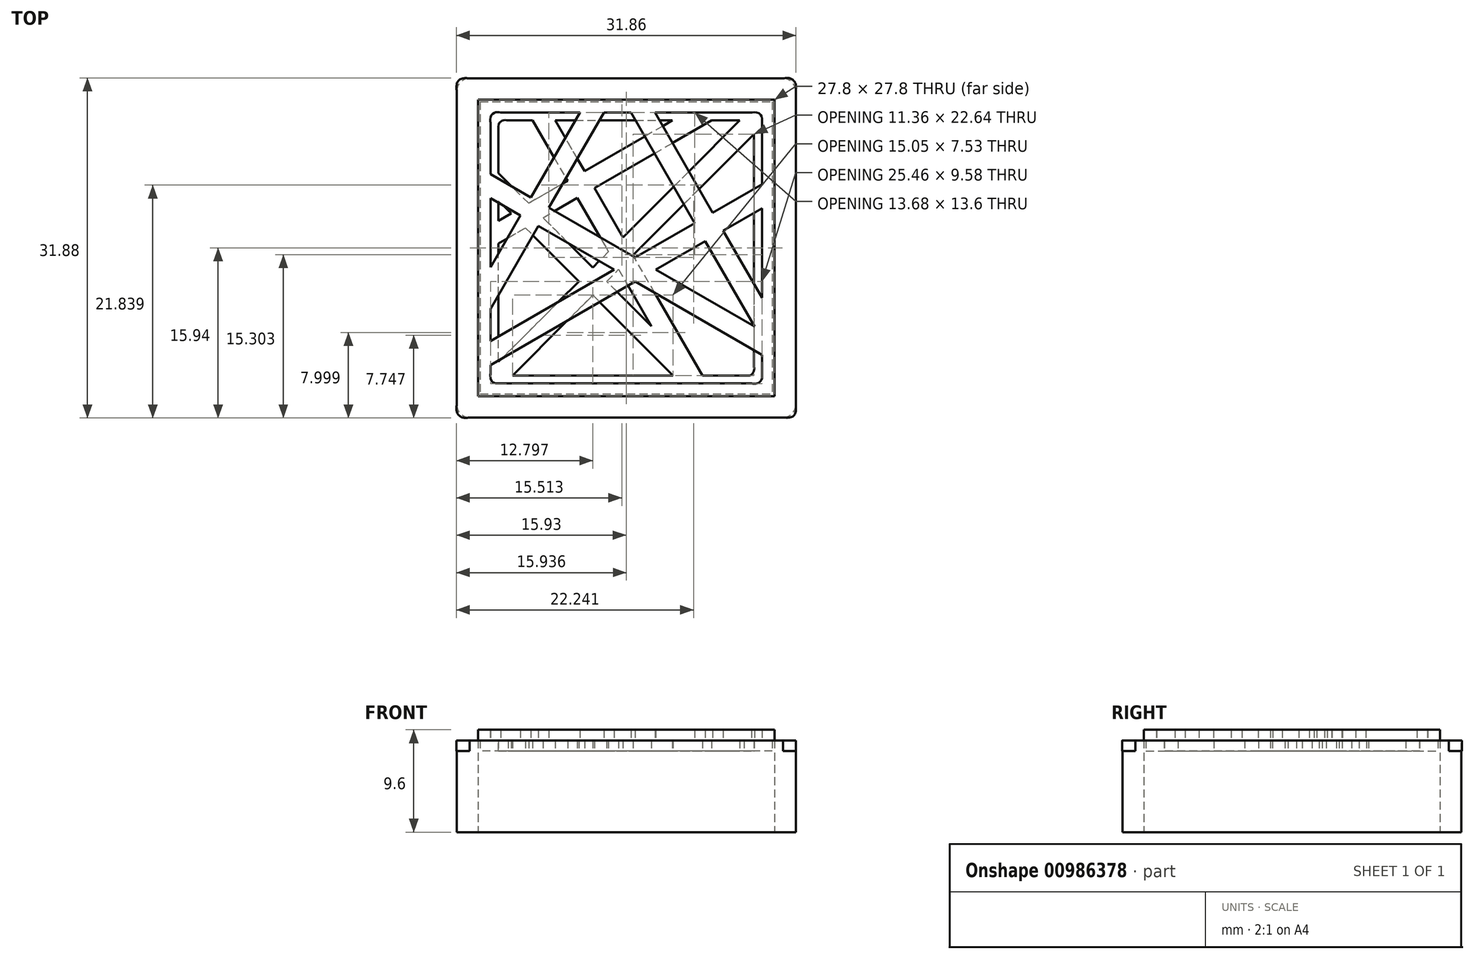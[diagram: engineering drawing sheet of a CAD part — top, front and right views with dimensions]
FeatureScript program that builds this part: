
annotation { "Feature Type Name" : "Feature", "Feature Type Description" : "" }
export const myFeature = defineFeature(function(context is Context, id is Id, definition is map)
    precondition{}
    {
        {
            var Q0;
            Q0=qCreatedBy(makeId("Top.planeOp"),FACE);
            var sketch = newSketch(context, id + "F0", { "sketchPlane" : qUnion([Q0])});
            skLineSegment(sketch, "E0", {"start": v(-12.72, 4.67) * mm, "end": v(-9.92, 3.05) * mm});
            skLineSegment(sketch, "E1", {"start": v(-9.92, 3.05) * mm, "end": v(-12.72, -1.8) * mm});
            skLineSegment(sketch, "E2", {"start": v(-12.72, -1.8) * mm, "end": v(-12.72, 4.67) * mm});
            skLineSegment(sketch, "E3", {"start": v(-12.72, -5.7) * mm, "end": v(-8.23, 2.08) * mm});
            skLineSegment(sketch, "E4", {"start": v(-8.23, 2.08) * mm, "end": v(-1.12, -2.03) * mm});
            skLineSegment(sketch, "E5", {"start": v(-1.12, -2.03) * mm, "end": v(-12.72, -8.72) * mm});
            skLineSegment(sketch, "E6", {"start": v(-12.72, -8.72) * mm, "end": v(-12.72, -5.7) * mm});
            skLineSegment(sketch, "E7", {"start": v(-7.26, 3.76) * mm, "end": v(-2.1, 12.7) * mm});
            skLineSegment(sketch, "E8", {"start": v(-2.1, 12.7) * mm, "end": v(0.44, 12.7) * mm});
            skLineSegment(sketch, "E9", {"start": v(0.44, 12.7) * mm, "end": v(6.43, 2.33) * mm});
            skLineSegment(sketch, "E10", {"start": v(6.43, 2.33) * mm, "end": v(0.82, -0.9) * mm});
            skLineSegment(sketch, "E11", {"start": v(0.82, -0.9) * mm, "end": v(-7.26, 3.76) * mm});
            skLineSegment(sketch, "E12", {"start": v(7.4, 0.64) * mm, "end": v(12.03, -7.37) * mm});
            skLineSegment(sketch, "E13", {"start": v(12.03, -7.37) * mm, "end": v(2.77, -2.03) * mm});
            skLineSegment(sketch, "E14", {"start": v(2.77, -2.03) * mm, "end": v(7.4, 0.64) * mm});
            skLineSegment(sketch, "E15", {"start": v(9.09, 1.62) * mm, "end": v(12.72, 3.72) * mm});
            skLineSegment(sketch, "E16", {"start": v(12.72, 3.72) * mm, "end": v(12.72, -4.68) * mm});
            skLineSegment(sketch, "E17", {"start": v(12.72, -4.68) * mm, "end": v(9.09, 1.62) * mm});
            skFitSpline(sketch, "E18", {"points": [v(12.72, 11.74) * mm, v(12.72, 11.74) * mm, v(12.72, 11.74) * mm, v(12.72, 11.6) * mm, v(12.72, 6.12) * mm, v(12.72, 5.97) * mm, v(12.72, 5.97) * mm, v(12.72, 5.97) * mm]});
            skFitSpline(sketch, "E19", {"points": [v(12.72, 5.97) * mm, v(12.72, 5.97) * mm, v(12.72, 5.97) * mm, v(12.6, 5.9) * mm, v(8.23, 3.37) * mm, v(8.11, 3.3) * mm, v(8.11, 3.3) * mm, v(8.11, 3.3) * mm]});
            skFitSpline(sketch, "E20", {"points": [v(8.11, 3.3) * mm, v(8.11, 3.3) * mm, v(8.11, 3.3) * mm, v(8.04, 3.43) * mm, v(6.72, 5.73) * mm, v(5.4, 8) * mm]});
            skFitSpline(sketch, "E21", {"points": [v(5.4, 8) * mm, v(4.09, 10.28) * mm, v(2.76, 12.58) * mm, v(2.7, 12.7) * mm, v(2.7, 12.7) * mm, v(2.7, 12.7) * mm]});
            skFitSpline(sketch, "E22", {"points": [v(2.7, 12.7) * mm, v(2.7, 12.7) * mm, v(2.7, 12.7) * mm, v(2.93, 12.7) * mm, v(11.72, 12.7) * mm, v(11.76, 12.7) * mm, v(11.77, 12.7) * mm, v(12.3, 12.7) * mm, v(12.72, 12.27) * mm, v(12.72, 11.74) * mm]});
            skFitSpline(sketch, "E23", {"points": [v(-11.76, 12.7) * mm, v(-11.76, 12.7) * mm, v(-11.76, 12.7) * mm, v(-11.57, 12.7) * mm, v(-4.54, 12.7) * mm, v(-4.35, 12.7) * mm, v(-4.35, 12.7) * mm, v(-4.35, 12.7) * mm]});
            skFitSpline(sketch, "E24", {"points": [v(-4.35, 12.7) * mm, v(-4.35, 12.7) * mm, v(-4.35, 12.7) * mm, v(-4.47, 12.5) * mm, v(-8.83, 4.94) * mm, v(-8.95, 4.74) * mm, v(-8.95, 4.74) * mm, v(-8.95, 4.74) * mm]});
            skFitSpline(sketch, "E25", {"points": [v(-8.95, 4.74) * mm, v(-8.95, 4.74) * mm, v(-8.95, 4.74) * mm, v(-9, 4.77) * mm, v(-9.92, 5.3) * mm, v(-10.84, 5.83) * mm]});
            skFitSpline(sketch, "E26", {"points": [v(-10.84, 5.83) * mm, v(-11.75, 6.36) * mm, v(-12.68, 6.9) * mm, v(-12.72, 6.92) * mm, v(-12.72, 6.92) * mm, v(-12.72, 6.92) * mm]});
            skFitSpline(sketch, "E27", {"points": [v(-12.72, 6.92) * mm, v(-12.72, 6.92) * mm, v(-12.72, 6.92) * mm, v(-12.72, 7.04) * mm, v(-12.72, 11.72) * mm, v(-12.72, 11.74) * mm, v(-12.72, 11.74) * mm, v(-12.72, 12.27) * mm, v(-12.29, 12.7) * mm, v(-11.76, 12.7) * mm]});
            skFitSpline(sketch, "E28", {"points": [v(11.76, -12.7) * mm, v(11.76, -12.7) * mm, v(11.76, -12.7) * mm, v(11.45, -12.7) * mm, v(-11.64, -12.7) * mm, v(-11.76, -12.7) * mm, v(-11.76, -12.7) * mm, v(-12.3, -12.7) * mm, v(-12.72, -12.27) * mm, v(-12.72, -11.74) * mm, v(-12.72, -11.74) * mm, v(-12.72, -11.73) * mm, v(-12.72, -11.05) * mm, v(-12.72, -10.98) * mm, v(-12.72, -10.98) * mm, v(-12.72, -10.97) * mm]});
            skFitSpline(sketch, "E29", {"points": [v(-12.72, -10.97) * mm, v(-12.72, -10.97) * mm, v(-12.72, -10.97) * mm, v(-12.64, -10.92) * mm, v(-9.28, -8.99) * mm, v(-5.95, -7.06) * mm]});
            skFitSpline(sketch, "E30", {"points": [v(-5.95, -7.06) * mm, v(-2.62, -5.14) * mm, v(0.74, -3.2) * mm, v(0.82, -3.15) * mm, v(0.82, -3.15) * mm, v(0.82, -3.15) * mm]});
            skFitSpline(sketch, "E31", {"points": [v(0.82, -3.15) * mm, v(0.82, -3.15) * mm, v(0.82, -3.15) * mm, v(0.98, -3.24) * mm, v(12.57, -9.93) * mm, v(12.72, -10.02) * mm, v(12.72, -10.02) * mm, v(12.72, -10.02) * mm]});
            skFitSpline(sketch, "E32", {"points": [v(12.72, -10.02) * mm, v(12.72, -10.02) * mm, v(12.72, -10.02) * mm, v(12.72, -10.11) * mm, v(12.72, -11.73) * mm, v(12.72, -11.74) * mm, v(12.72, -11.74) * mm, v(12.72, -12.27) * mm, v(12.29, -12.7) * mm, v(11.76, -12.7) * mm]});
            skLineSegment(sketch, "E33.bottom", {"start": v(-13.9, 15.9) * mm, "end": v(13.9, 15.9) * mm});
            skLineSegment(sketch, "E33.top", {"start": v(-13.9, -15.9) * mm, "end": v(13.9, -15.9) * mm});
            skLineSegment(sketch, "E33.left", {"start": v(-15.9, 13.9) * mm, "end": v(-15.9, -13.9) * mm});
            skLineSegment(sketch, "E33.right", {"start": v(15.9, 13.9) * mm, "end": v(15.9, -13.9) * mm});
            skPoint(sketch, "E33.middle", {"position": v(0, 0) * mm});
            skPoint(sketch, "E34.visualSharp", {"position": v(-15.9, 15.9) * mm});
            skArc(sketch, "E34.filletArc", {"start": v(-13.9, 15.9) * mm, "mid": v(-15.31, 15.31) * mm, "end": v(-15.9, 13.9) * mm});
            skPoint(sketch, "E35.visualSharp", {"position": v(15.9, 15.9) * mm});
            skArc(sketch, "E35.filletArc", {"start": v(15.9, 13.9) * mm, "mid": v(15.31, 15.31) * mm, "end": v(13.9, 15.9) * mm});
            skPoint(sketch, "E36.visualSharp", {"position": v(15.9, -15.9) * mm});
            skArc(sketch, "E36.filletArc", {"start": v(13.9, -15.9) * mm, "mid": v(15.31, -15.31) * mm, "end": v(15.9, -13.9) * mm});
            skPoint(sketch, "E37.visualSharp", {"position": v(-15.9, -15.9) * mm});
            skArc(sketch, "E37.filletArc", {"start": v(-15.9, -13.9) * mm, "mid": v(-15.31, -15.31) * mm, "end": v(-13.9, -15.9) * mm});
            skSolve(sketch);
        }
        {
            var Q0;
            Q0=makeQuery(id+"F0.imprint","IMPRINT",FACE,{"disambiguationData":[TD([[makeQuery(id+"F0.imprint","IMPRINT",EDGE,{"derivedFrom":sQuery(id+"F0.wireOp",EDGE,"E0")}),1.0]])]});
            extrude(context, id + "F1", {"entities" : qUnion([Q0]), "depth" : 9.6 * mm, "offsetDistance" : 25 * mm, "hasSecondDirection" : true, "secondDirectionOppositeDirection" : false, "secondDirectionDepth" : 8.6 * mm});
        }
        {
            var Q0;
            Q0=qCreatedBy(makeId("Top.planeOp"),FACE);
            var sketch = newSketch(context, id + "F2", { "sketchPlane" : qUnion([Q0])});
            skLineSegment(sketch, "E38", {"start": v(-11.98, 4.42) * mm, "end": v(-10.79, 3.23) * mm});
            skLineSegment(sketch, "E39", {"start": v(-10.79, 3.23) * mm, "end": v(-11.98, 2.54) * mm});
            skLineSegment(sketch, "E40", {"start": v(-11.98, 2.54) * mm, "end": v(-11.98, 4.42) * mm});
            skLineSegment(sketch, "E41", {"start": v(-11.98, 0.42) * mm, "end": v(-9.45, 1.88) * mm});
            skLineSegment(sketch, "E42", {"start": v(-9.45, 1.88) * mm, "end": v(-4.43, -3.13) * mm});
            skLineSegment(sketch, "E43", {"start": v(-4.43, -3.13) * mm, "end": v(-11.98, -10.68) * mm});
            skLineSegment(sketch, "E44", {"start": v(-11.98, -10.68) * mm, "end": v(-11.98, 0.42) * mm});
            skLineSegment(sketch, "E45", {"start": v(-3.13, -4.43) * mm, "end": v(4.4, -11.96) * mm});
            skLineSegment(sketch, "E46", {"start": v(4.4, -11.96) * mm, "end": v(-10.66, -11.96) * mm});
            skLineSegment(sketch, "E47", {"start": v(-10.66, -11.96) * mm, "end": v(-3.13, -4.43) * mm});
            skLineSegment(sketch, "E48", {"start": v(-1.84, -3.13) * mm, "end": v(-0.71, -2) * mm});
            skLineSegment(sketch, "E49", {"start": v(-0.71, -2) * mm, "end": v(2.36, -7.33) * mm});
            skLineSegment(sketch, "E50", {"start": v(2.36, -7.33) * mm, "end": v(-1.84, -3.13) * mm});
            skLineSegment(sketch, "E51", {"start": v(-3.13, -1.84) * mm, "end": v(-7.8, 2.83) * mm});
            skLineSegment(sketch, "E52", {"start": v(-7.8, 2.83) * mm, "end": v(-4.58, 4.7) * mm});
            skLineSegment(sketch, "E53", {"start": v(-4.58, 4.7) * mm, "end": v(-1.66, -0.36) * mm});
            skLineSegment(sketch, "E54", {"start": v(-1.66, -0.36) * mm, "end": v(-3.13, -1.84) * mm});
            skLineSegment(sketch, "E55", {"start": v(-3, 5.61) * mm, "end": v(8, 11.96) * mm});
            skLineSegment(sketch, "E56", {"start": v(8, 11.96) * mm, "end": v(10.66, 11.96) * mm});
            skLineSegment(sketch, "E57", {"start": v(10.66, 11.96) * mm, "end": v(-0.32, 0.98) * mm});
            skLineSegment(sketch, "E58", {"start": v(-0.32, 0.98) * mm, "end": v(-3, 5.61) * mm});
            skLineSegment(sketch, "E59", {"start": v(-3.9, 7.2) * mm, "end": v(-6.66, 11.96) * mm});
            skLineSegment(sketch, "E60", {"start": v(-6.66, 11.96) * mm, "end": v(4.33, 11.96) * mm});
            skLineSegment(sketch, "E61", {"start": v(4.33, 11.96) * mm, "end": v(-3.9, 7.2) * mm});
            skFitSpline(sketch, "E62", {"points": [v(14.7, 15.9) * mm, v(14.7, 15.9) * mm, v(14.7, 15.9) * mm, v(14.31, 15.9) * mm, v(-14.62, 15.9) * mm, v(-14.7, 15.9) * mm, v(-14.7, 15.9) * mm, v(-15.36, 15.9) * mm, v(-15.9, 15.36) * mm, v(-15.9, 14.7) * mm, v(-15.9, 14.7) * mm, v(-15.9, 14.62) * mm, v(-15.9, -14.64) * mm, v(-15.9, -14.7) * mm, v(-15.9, -14.7) * mm, v(-15.9, -15.36) * mm, v(-15.36, -15.9) * mm, v(-14.7, -15.9) * mm]});
            skFitSpline(sketch, "E63", {"points": [v(-14.7, -15.9) * mm, v(-14.7, -15.9) * mm, v(-14.7, -15.9) * mm, v(-14.31, -15.9) * mm, v(14.62, -15.9) * mm, v(14.7, -15.9) * mm, v(14.7, -15.9) * mm, v(15.36, -15.9) * mm, v(15.9, -15.36) * mm, v(15.9, -14.7) * mm, v(15.9, -14.7) * mm, v(15.9, -14.62) * mm, v(15.9, 14.64) * mm, v(15.9, 14.7) * mm, v(15.9, 14.7) * mm, v(15.9, 15.36) * mm, v(15.36, 15.9) * mm, v(14.7, 15.9) * mm]});
            skFitSpline(sketch, "E64", {"points": [v(-11.07, 11.96) * mm, v(-11.07, 11.96) * mm, v(-11.07, 11.96) * mm, v(-10.95, 11.96) * mm, v(-8.89, 11.96) * mm, v(-8.78, 11.96) * mm, v(-8.78, 11.96) * mm, v(-8.77, 11.96) * mm]});
            skFitSpline(sketch, "E65", {"points": [v(-8.77, 11.96) * mm, v(-8.77, 11.96) * mm, v(-8.77, 11.96) * mm, v(-8.7, 11.81) * mm, v(-5.58, 6.43) * mm, v(-5.5, 6.28) * mm, v(-5.5, 6.28) * mm, v(-5.5, 6.28) * mm]});
            skFitSpline(sketch, "E66", {"points": [v(-5.5, 6.28) * mm, v(-5.5, 6.28) * mm, v(-5.5, 6.28) * mm, v(-5.6, 6.23) * mm, v(-9.05, 4.23) * mm, v(-9.14, 4.18) * mm, v(-9.14, 4.18) * mm, v(-9.15, 4.18) * mm]});
            skFitSpline(sketch, "E67", {"points": [v(-9.15, 4.18) * mm, v(-9.15, 4.18) * mm, v(-9.15, 4.18) * mm, v(-9.22, 4.25) * mm, v(-11.9, 6.94) * mm, v(-11.98, 7) * mm, v(-11.98, 7) * mm, v(-11.98, 7) * mm]});
            skFitSpline(sketch, "E68", {"points": [v(-11.98, 7) * mm, v(-11.98, 7.01) * mm, v(-11.98, 7.01) * mm, v(-11.98, 7.11) * mm, v(-11.98, 11.03) * mm, v(-11.98, 11.05) * mm, v(-11.98, 11.05) * mm, v(-11.97, 11.55) * mm, v(-11.57, 11.96) * mm, v(-11.07, 11.96) * mm]});
            skFitSpline(sketch, "E69", {"points": [v(11.07, -11.96) * mm, v(11.07, -11.96) * mm, v(11.07, -11.96) * mm, v(10.97, -11.96) * mm, v(7.25, -11.96) * mm, v(7.15, -11.96) * mm, v(7.15, -11.96) * mm, v(7.15, -11.96) * mm]});
            skFitSpline(sketch, "E70", {"points": [v(7.15, -11.96) * mm, v(7.15, -11.96) * mm, v(7.15, -11.96) * mm, v(7.07, -11.81) * mm, v(0.72, -0.81) * mm, v(0.63, -0.67) * mm, v(0.63, -0.67) * mm, v(0.63, -0.67) * mm]});
            skFitSpline(sketch, "E71", {"points": [v(0.63, -0.67) * mm, v(0.63, -0.67) * mm, v(0.63, -0.67) * mm, v(0.7, -0.6) * mm, v(3.51, 2.22) * mm, v(6.3, 5) * mm]});
            skFitSpline(sketch, "E72", {"points": [v(6.3, 5) * mm, v(9.1, 7.8) * mm, v(11.9, 10.6) * mm, v(11.98, 10.68) * mm, v(11.98, 10.68) * mm, v(11.98, 10.68) * mm]});
            skFitSpline(sketch, "E73", {"points": [v(11.98, 10.68) * mm, v(11.98, 10.68) * mm, v(11.98, 10.68) * mm, v(11.98, 10.4) * mm, v(11.98, -10.96) * mm, v(11.98, -11.05) * mm, v(11.98, -11.05) * mm, v(11.97, -11.55) * mm, v(11.57, -11.96) * mm, v(11.07, -11.96) * mm]});
            skSolve(sketch);
        }
        {
            var Q0;
            Q0 = qSketchRegion(id + "F2", true);
            extrude(context, id + "F3", {"entities" : qUnion([Q0]), "depth" : 8.6 * mm, "offsetDistance" : 25 * mm, "hasSecondDirection" : true, "secondDirectionOppositeDirection" : false, "secondDirectionDepth" : 7.6 * mm});
        }
        {
            var Q0;
            Q0=qCreatedBy(makeId("Top.planeOp"),FACE);
            var sketch = newSketch(context, id + "F4", { "sketchPlane" : qUnion([Q0])});
            skLineSegment(sketch, "E74.bottom", {"start": v(-14.7, 15.9) * mm, "end": v(14.7, 15.9) * mm});
            skLineSegment(sketch, "E74.top", {"start": v(-14.7, -15.9) * mm, "end": v(14.7, -15.9) * mm});
            skLineSegment(sketch, "E74.left", {"start": v(-15.9, 14.7) * mm, "end": v(-15.9, -14.7) * mm});
            skLineSegment(sketch, "E74.right", {"start": v(15.9, 14.7) * mm, "end": v(15.9, -14.7) * mm});
            skPoint(sketch, "E74.middle", {"position": v(0, 0) * mm});
            skPoint(sketch, "E75.visualSharp", {"position": v(-15.9, 15.9) * mm});
            skArc(sketch, "E75.filletArc", {"start": v(-14.7, 15.9) * mm, "mid": v(-15.55, 15.55) * mm, "end": v(-15.9, 14.7) * mm});
            skPoint(sketch, "E76.visualSharp", {"position": v(15.9, 15.9) * mm});
            skArc(sketch, "E76.filletArc", {"start": v(15.9, 14.7) * mm, "mid": v(15.55, 15.55) * mm, "end": v(14.7, 15.9) * mm});
            skPoint(sketch, "E77.visualSharp", {"position": v(15.9, -15.9) * mm});
            skArc(sketch, "E77.filletArc", {"start": v(14.7, -15.9) * mm, "mid": v(15.55, -15.55) * mm, "end": v(15.9, -14.7) * mm});
            skPoint(sketch, "E78.visualSharp", {"position": v(-15.9, -15.9) * mm});
            skArc(sketch, "E78.filletArc", {"start": v(-15.9, -14.7) * mm, "mid": v(-15.55, -15.55) * mm, "end": v(-14.7, -15.9) * mm});
            skLineSegment(sketch, "E79.0", {"start": v(-13.9, 13.9) * mm, "end": v(13.9, 13.9) * mm});
            skLineSegment(sketch, "E79.1", {"start": v(-13.9, 13.9) * mm, "end": v(-13.9, -13.9) * mm});
            skLineSegment(sketch, "E79.2", {"start": v(-13.9, -13.9) * mm, "end": v(13.9, -13.9) * mm});
            skLineSegment(sketch, "E79.3", {"start": v(13.9, 13.9) * mm, "end": v(13.9, -13.9) * mm});
            skSolve(sketch);
        }
        {
            var Q0;
            Q0 = qSketchRegion(id + "F4", true);
            extrude(context, id + "F5", {"entities" : qUnion([Q0]), "operationType" : NewBodyOperationType.REMOVE, "endBound" : BoundingType.THROUGH_ALL, "depth" : 9.6 * mm, "offsetDistance" : 25 * mm});
        }
        {
            var Q0;
            Q0=qCreatedBy(makeId("Top.planeOp"),FACE);
            var sketch = newSketch(context, id + "F6", { "sketchPlane" : qUnion([Q0])});
            skLineSegment(sketch, "E80.bottom", {"start": v(-14.7, 15.9) * mm, "end": v(14.7, 15.9) * mm});
            skLineSegment(sketch, "E80.top", {"start": v(-14.7, -15.9) * mm, "end": v(14.7, -15.9) * mm});
            skLineSegment(sketch, "E80.left", {"start": v(-15.9, 14.7) * mm, "end": v(-15.9, -14.7) * mm});
            skLineSegment(sketch, "E80.right", {"start": v(15.9, 14.7) * mm, "end": v(15.9, -14.7) * mm});
            skPoint(sketch, "E80.middle", {"position": v(0, 0) * mm});
            skPoint(sketch, "E81.visualSharp", {"position": v(-15.9, 15.9) * mm});
            skArc(sketch, "E81.filletArc", {"start": v(-14.7, 15.9) * mm, "mid": v(-15.55, 15.55) * mm, "end": v(-15.9, 14.7) * mm});
            skPoint(sketch, "E82.visualSharp", {"position": v(15.9, 15.9) * mm});
            skArc(sketch, "E82.filletArc", {"start": v(15.9, 14.7) * mm, "mid": v(15.55, 15.55) * mm, "end": v(14.7, 15.9) * mm});
            skPoint(sketch, "E83.visualSharp", {"position": v(15.9, -15.9) * mm});
            skArc(sketch, "E83.filletArc", {"start": v(14.7, -15.9) * mm, "mid": v(15.55, -15.55) * mm, "end": v(15.9, -14.7) * mm});
            skPoint(sketch, "E84.visualSharp", {"position": v(-15.9, -15.9) * mm});
            skArc(sketch, "E84.filletArc", {"start": v(-15.9, -14.7) * mm, "mid": v(-15.55, -15.55) * mm, "end": v(-14.7, -15.9) * mm});
            skLineSegment(sketch, "E85.0", {"start": v(-13.7, 13.7) * mm, "end": v(13.7, 13.7) * mm});
            skLineSegment(sketch, "E85.1", {"start": v(-13.7, 13.7) * mm, "end": v(-13.7, -13.7) * mm});
            skLineSegment(sketch, "E85.2", {"start": v(-13.7, -13.7) * mm, "end": v(13.7, -13.7) * mm});
            skLineSegment(sketch, "E85.3", {"start": v(13.7, 13.7) * mm, "end": v(13.7, -13.7) * mm});
            skSolve(sketch);
        }
        {
            var Q0;
            Q0 = qSketchRegion(id + "F6", true);
            extrude(context, id + "F7", {"entities" : qUnion([Q0]), "operationType" : NewBodyOperationType.REMOVE, "depth" : 8.6 * mm, "offsetDistance" : 25 * mm});
        }
        {
            var Q0;
            Q0 = qSketchRegion(id + "F4", true);
            extrude(context, id + "F8", {"entities" : qUnion([Q0]), "operationType" : NewBodyOperationType.ADD, "depth" : 8.6 * mm, "offsetDistance" : 25 * mm});
        }
    });
